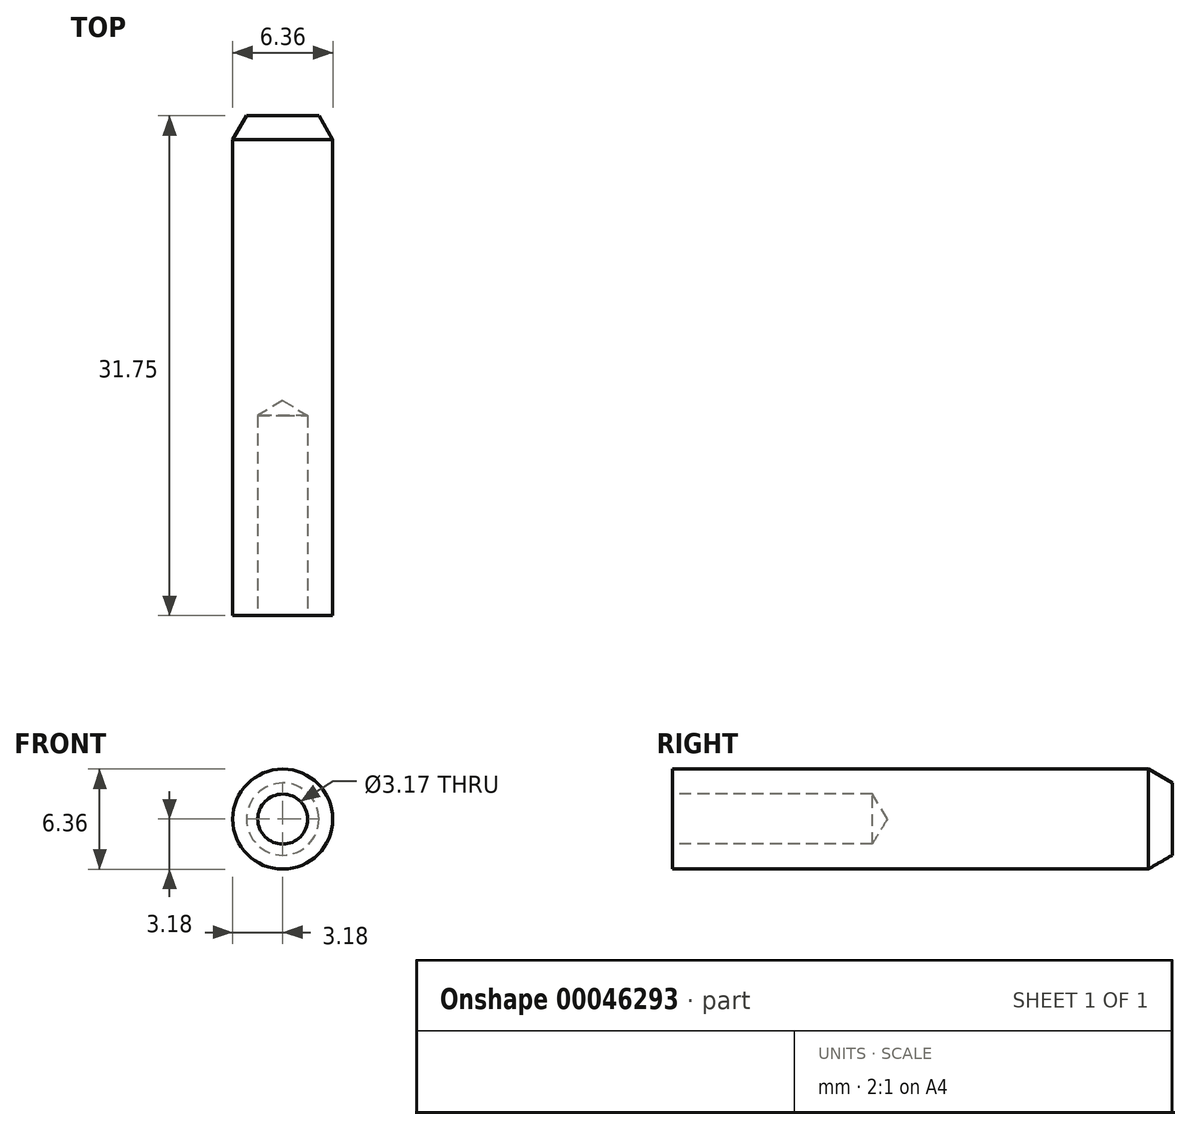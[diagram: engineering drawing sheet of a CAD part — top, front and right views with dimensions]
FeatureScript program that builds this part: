
annotation { "Feature Type Name" : "Feature", "Feature Type Description" : "" }
export const myFeature = defineFeature(function(context is Context, id is Id, definition is map)
    precondition{}
    {
        {
            var Q0;
            Q0=qCreatedBy(makeId("Front.planeOp"),FACE);
            var sketch = newSketch(context, id + "F0", { "sketchPlane" : qUnion([Q0])});
            skCircle(sketch, "E0", {"center": v(0, 0) * mm, "radius": 3.18 * mm});
            skSolve(sketch);
        }
        {
            var Q0;
            Q0=makeQuery(id+"F0.imprint","IMPRINT",FACE,{"disambiguationData":[TD([[makeQuery(id+"F0.imprint","IMPRINT",EDGE,{"derivedFrom":sQuery(id+"F0.wireOp",EDGE,"E0")}),1.0]])]});
            extrude(context, id + "F1", {"entities" : qUnion([Q0]), "depth" : 31.75 * mm});
        }
        {
            var Q0;
            Q0=makeQuery(id+"F1.opExtrude","CAP_FACE",FACE,{"disambiguationData":[OSD([sQuery(id+"F0.wireOp",EDGE,"E0")])],"isStart":false});
            var sketch = newSketch(context, id + "F2", { "sketchPlane" : qUnion([Q0])});
            skPoint(sketch, "E1", {"position": v(0, 0) * mm});
            skSolve(sketch);
        }
        {
            var Q0;
            Q0=sQuery(id+"F2.wireOp",VERTEX,"E1");
            var Q1;
            Q1=makeQuery(id+"F1.opExtrude","SWEPT_BODY",BODY,{"disambiguationData":[OSD([sQuery(id+"F0.wireOp",EDGE,"E0")])]});
            hole(context, id + "F3", {"style" : HoleStyle.SIMPLE, "holeDiameter" : 3.17 * mm, "endStyle" : HoleEndStyle.BLIND, "holeDepth" : 12.7 * mm, "locations" : qUnion([Q0]), "scope" : qUnion([Q1])});
        }
        {
            var Q0;
            Q0=makeQuery(id+"F1.opExtrude","CAP_EDGE",EDGE,{"disambiguationData":[OSD([sQuery(id+"F0.wireOp",EDGE,"E0")])],"isStart":true});
            chamfer(context, id + "F4", {"entities" : qUnion([Q0]), "chamferType" : ChamferType.OFFSET_ANGLE, "width" : 1.52 * mm, "oppositeDirection" : false, "angle" : 30 * degree, "tangentPropagation" : true});
        }
    });
